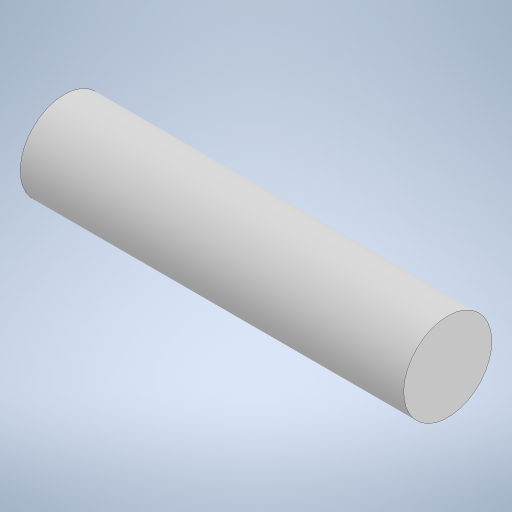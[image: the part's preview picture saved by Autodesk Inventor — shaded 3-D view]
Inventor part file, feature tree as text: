
AUTODESK INVENTOR PART (.ipt)
format: ipt  version: 2023 (Build 270158000, 158)  size: 212,480 bytes
history: native  units: in
note: dims shown in document units (in); Inventor stores cm internally (conversion verified against a paired STEP export)
features: extrude x1, sketch x1
ambient origin geometry x8: Origin, YZ Plane, XZ Plane, XY Plane, X Axis, Y Axis, Z Axis, Center Point
bodies: Solid1 (feature_tree)
feature tree (2):
  extrude  "Extrusion1"  Depth=0.34in TaperAngle=0.0deg
  sketch  "Sketch1"  dims[d0=0.0781in d1=0.34in d2=0.0in]
